# Revit family: Sanitary_Shower-screens_Duscholux_Pure-Style_Andromeda_Separator_Fixed-panel-shower-bath
name_source: partatom
category: Plumbing Fixtures
revit_build: Autodesk Revit 2016 (Build: 20150220_1215(x64)
units: mm (PartAtom-declared; Revit-internal decimal feet)

## family parameters
Always vertical = Yes
Cut with Voids When Loaded = No
OmniClass Number = 23.45.00.00
OmniClass Title = Sanitary, Laundry, and Cleaning Equipment
Part Type = Normal
Room Calculation Point = No
Round Connector Dimension = Use Diameter
Shared = No
Work Plane-Based = No

## types (2) — shared parameters
Accesories Material = Chrome_Finish
Assembly Code = C1030200
Brand = Duscholux
Certified Quality UNE EN 14428 = http://www.duscholux.es
Combinations = Hinge and handle to choice (Round, square or triangular)
Components = Eropean components
Configuration enclosure = http://configuratumampara.duscholux.es
Description = Fixed panel for shower
Design country = Spain / Germany
Edition number = 1
Environmental Management ISO 14001 = ECOEMBES Certificate
Fact Sheet = http://blob.duscholux.es
Glass Material = Glass_Material-Duscholux
Glass in Building UNE EN 12150 = CE Conformity marking
Handle Material = Chrome_Finish
IFC Classification = Furnishing Element
Image = https://www.duscholux.es
Lenght Support = 800 mm  [stored 2.62467 ft]
Maintenance and Cleaning = http://www.duscholux.es
Manufacturer = Duscholux Ibérica, S.A.
Manufacturer country = Spain
Manufacturer name = Duscholux Ibérica, S.A.
Model = Andromeda
NBS Reference Code = 45-35-70
NBS Reference Description = Shower Enclosures
Net Weight (Kg) = 53.5
Opening System = Pivot Door
Opening System Image = http://blob.duscholux.es
Product family = Pure Style
Product group = Fixed panel
Products = http://www.duscholux.es
Ref. = 41I / 41D
Series = Pure Style
Technical Inspection Certificate (Applus) = http://www.duscholux.es
Thickness Glass = 8 mm  [stored 0.0262467 ft]
UNSPSC Code = 30181507
URL = http://www.duscholux.es
Uniclass 2015 Code = PR-40-20-06-79
Uniclass 2015 Description = Shower Enclosures

## per-type parameters (varying)
| type | Height | Max Height | Min Max Width | Offset Support | Width |
| Silver Matt Aluminium Finish | 1800 mm  [stored 5.90551 ft] | 1800 mm  [stored 5.90551 ft] | 900 mm  [stored 2.95276 ft] | 100 mm  [stored 0.328084 ft] | 900 mm  [stored 2.95276 ft] |
| Platinum Aluminium Finish | 1900 mm  [stored 6.2336 ft] | 1900 mm  [stored 6.2336 ft] | 1000 mm  [stored 3.28084 ft] | 150 mm | 1000 mm  [stored 3.28084 ft] |

note: column(s) folded — value = type name in every type: Frame Material

note: [stored X ft] marks values corroborated as IEEE doubles in the binary element streams (Revit-internal decimal feet)

## geometry (parser evidence)
native form markers: Sweep x3
no freeform markers — native parametric forms only
